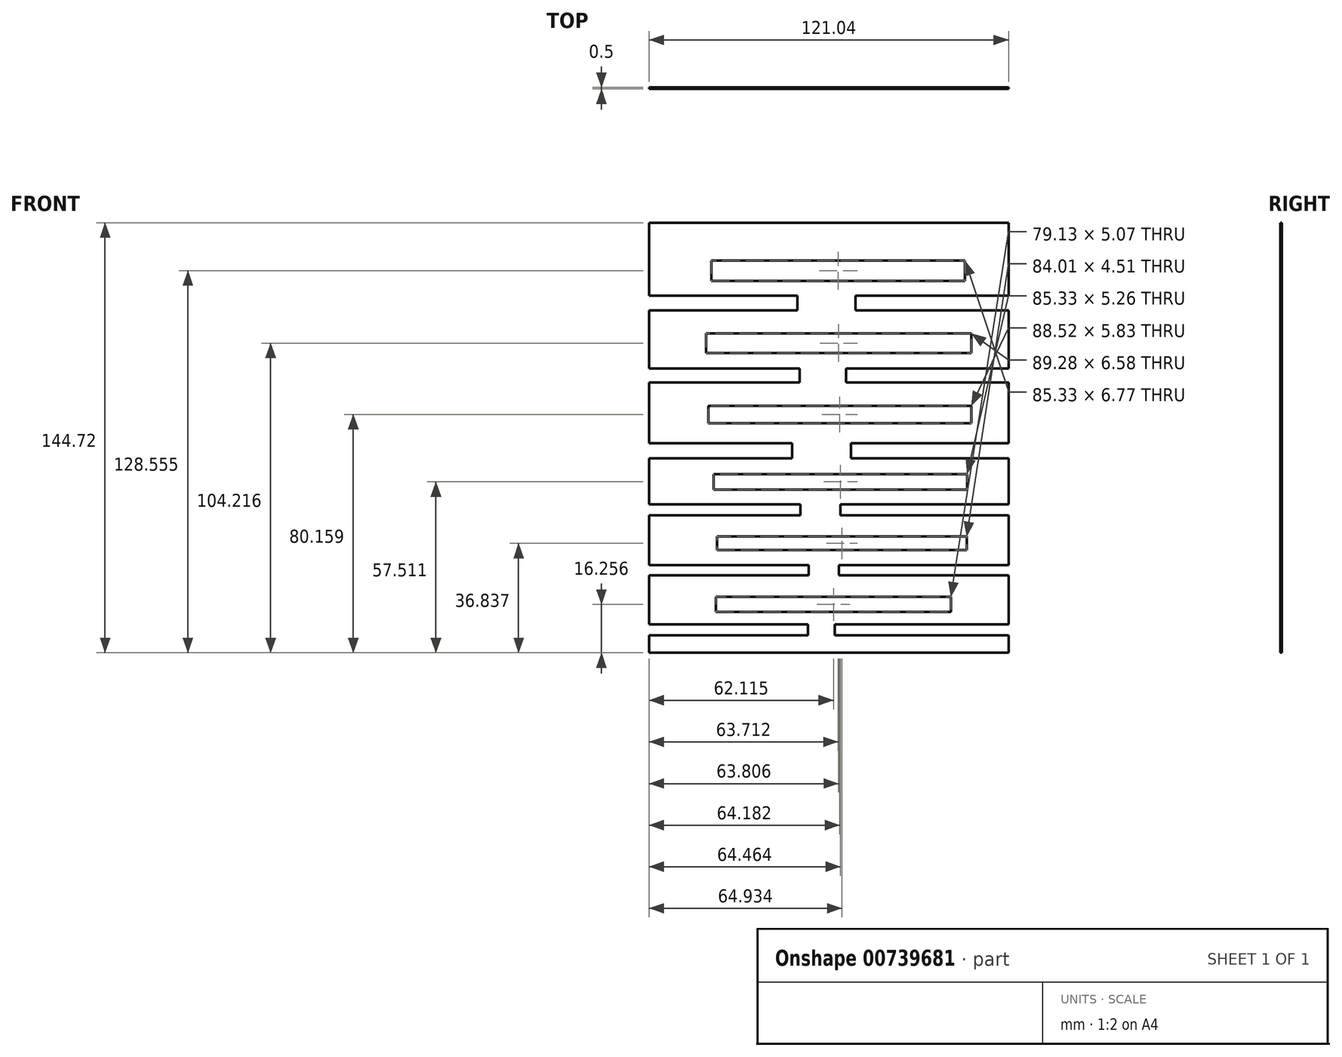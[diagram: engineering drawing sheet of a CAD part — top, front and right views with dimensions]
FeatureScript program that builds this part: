
annotation { "Feature Type Name" : "Feature", "Feature Type Description" : "" }
export const myFeature = defineFeature(function(context is Context, id is Id, definition is map)
    precondition{}
    {
        {
            var Q0;
            Q0=qCreatedBy(makeId("Front.planeOp"),FACE);
            var sketch = newSketch(context, id + "F0", { "sketchPlane" : qUnion([Q0])});
            skLineSegment(sketch, "E0.bottom", {"start": v(-58.36, 71.9) * mm, "end": v(62.68, 71.9) * mm});
            skLineSegment(sketch, "E0.top", {"start": v(-58.36, -72.82) * mm, "end": v(62.68, -72.82) * mm});
            skLineSegment(sketch, "E0.left", {"start": v(-58.36, 71.9) * mm, "end": v(-58.36, 47.37) * mm});
            skLineSegment(sketch, "E0.right", {"start": v(62.68, 71.9) * mm, "end": v(62.68, 47.37) * mm});
            skLineSegment(sketch, "E1.bottom", {"start": v(-58.36, -63.24) * mm, "end": v(-4.8, -63.24) * mm});
            skLineSegment(sketch, "E1.top", {"start": v(-58.36, -67) * mm, "end": v(-4.8, -67) * mm});
            skLineSegment(sketch, "E2", {"start": v(-4.8, -63.24) * mm, "end": v(-4.8, -67) * mm});
            skLineSegment(sketch, "E3", {"start": v(4.22, -63.24) * mm, "end": v(4.22, -67) * mm});
            skLineSegment(sketch, "E4.trimOffspring", {"start": v(4.22, -67) * mm, "end": v(62.68, -67) * mm});
            skLineSegment(sketch, "E5.trimOffspring", {"start": v(4.22, -63.24) * mm, "end": v(62.68, -63.24) * mm});
            skLineSegment(sketch, "E6.trimOffspring", {"start": v(-58.36, -67) * mm, "end": v(-58.36, -72.82) * mm});
            skLineSegment(sketch, "E7.trimOffspring", {"start": v(62.68, -67) * mm, "end": v(62.68, -72.82) * mm});
            skLineSegment(sketch, "E8.bottom", {"start": v(-35.8, -54.03) * mm, "end": v(43.32, -54.03) * mm});
            skLineSegment(sketch, "E8.top", {"start": v(-35.8, -59.1) * mm, "end": v(43.32, -59.1) * mm});
            skLineSegment(sketch, "E8.left", {"start": v(-35.8, -54.03) * mm, "end": v(-35.8, -59.1) * mm});
            skLineSegment(sketch, "E8.right", {"start": v(43.32, -54.03) * mm, "end": v(43.32, -59.1) * mm});
            skLineSegment(sketch, "E9.bottom", {"start": v(-58.36, -46.7) * mm, "end": v(-4.6, -46.7) * mm});
            skLineSegment(sketch, "E9.top", {"start": v(-58.36, -43.31) * mm, "end": v(-4.6, -43.31) * mm});
            skLineSegment(sketch, "E10", {"start": v(-4.6, -43.31) * mm, "end": v(-4.6, -46.7) * mm});
            skLineSegment(sketch, "E11", {"start": v(5.54, -43.31) * mm, "end": v(5.54, -46.7) * mm});
            skLineSegment(sketch, "E12.trimOffspring", {"start": v(5.54, -46.7) * mm, "end": v(62.68, -46.7) * mm});
            skLineSegment(sketch, "E13.trimOffspring", {"start": v(5.54, -43.31) * mm, "end": v(62.68, -43.31) * mm});
            skLineSegment(sketch, "E14.trimOffspring", {"start": v(-58.36, -46.7) * mm, "end": v(-58.36, -63.24) * mm});
            skLineSegment(sketch, "E15.trimOffspring", {"start": v(62.68, -46.7) * mm, "end": v(62.68, -63.24) * mm});
            skLineSegment(sketch, "E16.bottom", {"start": v(-35.43, -33.73) * mm, "end": v(48.58, -33.73) * mm});
            skLineSegment(sketch, "E16.top", {"start": v(-35.43, -38.24) * mm, "end": v(48.58, -38.24) * mm});
            skLineSegment(sketch, "E16.left", {"start": v(-35.43, -33.73) * mm, "end": v(-35.43, -38.24) * mm});
            skLineSegment(sketch, "E16.right", {"start": v(48.58, -33.73) * mm, "end": v(48.58, -38.24) * mm});
            skLineSegment(sketch, "E17.bottom", {"start": v(-58.36, -26.59) * mm, "end": v(-7.43, -26.59) * mm});
            skLineSegment(sketch, "E17.top", {"start": v(-58.36, -22.83) * mm, "end": v(-7.43, -22.83) * mm});
            skLineSegment(sketch, "E18", {"start": v(-7.43, -22.83) * mm, "end": v(-7.43, -26.59) * mm});
            skLineSegment(sketch, "E19", {"start": v(6.1, -22.83) * mm, "end": v(6.1, -26.59) * mm});
            skLineSegment(sketch, "E20.trimOffspring", {"start": v(6.1, -26.59) * mm, "end": v(62.68, -26.59) * mm});
            skLineSegment(sketch, "E21.trimOffspring", {"start": v(6.1, -22.83) * mm, "end": v(62.68, -22.83) * mm});
            skLineSegment(sketch, "E22.trimOffspring", {"start": v(-58.36, -26.59) * mm, "end": v(-58.36, -43.31) * mm});
            skLineSegment(sketch, "E23.trimOffspring", {"start": v(62.68, -26.59) * mm, "end": v(62.68, -43.31) * mm});
            skLineSegment(sketch, "E24.bottom", {"start": v(-36.56, -12.68) * mm, "end": v(48.77, -12.68) * mm});
            skLineSegment(sketch, "E24.top", {"start": v(-36.56, -17.94) * mm, "end": v(48.77, -17.94) * mm});
            skLineSegment(sketch, "E24.left", {"start": v(-36.56, -12.68) * mm, "end": v(-36.56, -17.94) * mm});
            skLineSegment(sketch, "E24.right", {"start": v(48.77, -12.68) * mm, "end": v(48.77, -17.94) * mm});
            skLineSegment(sketch, "E25.bottom", {"start": v(-58.36, -2.34) * mm, "end": v(-10.25, -2.34) * mm});
            skLineSegment(sketch, "E25.top", {"start": v(-58.36, -7.42) * mm, "end": v(-10.25, -7.42) * mm});
            skLineSegment(sketch, "E26", {"start": v(-10.25, -2.34) * mm, "end": v(-10.25, -7.42) * mm});
            skLineSegment(sketch, "E27", {"start": v(9.68, -2.34) * mm, "end": v(9.68, -7.42) * mm});
            skLineSegment(sketch, "E28.trimOffspring", {"start": v(9.68, -7.42) * mm, "end": v(62.68, -7.42) * mm});
            skLineSegment(sketch, "E29.trimOffspring", {"start": v(9.68, -2.34) * mm, "end": v(62.68, -2.34) * mm});
            skLineSegment(sketch, "E30.trimOffspring", {"start": v(-58.36, -7.42) * mm, "end": v(-58.36, -22.83) * mm});
            skLineSegment(sketch, "E31.trimOffspring", {"start": v(62.68, -7.42) * mm, "end": v(62.68, -22.83) * mm});
            skLineSegment(sketch, "E32.bottom", {"start": v(-38.44, 10.25) * mm, "end": v(50.08, 10.25) * mm});
            skLineSegment(sketch, "E32.top", {"start": v(-38.44, 4.43) * mm, "end": v(50.08, 4.43) * mm});
            skLineSegment(sketch, "E32.left", {"start": v(-38.44, 10.25) * mm, "end": v(-38.44, 4.43) * mm});
            skLineSegment(sketch, "E32.right", {"start": v(50.08, 10.25) * mm, "end": v(50.08, 4.43) * mm});
            skLineSegment(sketch, "E33.bottom", {"start": v(-58.36, 22.84) * mm, "end": v(-7.62, 22.84) * mm});
            skLineSegment(sketch, "E33.top", {"start": v(-58.36, 18.15) * mm, "end": v(-7.62, 18.15) * mm});
            skLineSegment(sketch, "E34", {"start": v(-7.62, 22.84) * mm, "end": v(-7.62, 18.15) * mm});
            skLineSegment(sketch, "E35", {"start": v(7.98, 22.84) * mm, "end": v(7.98, 18.15) * mm});
            skLineSegment(sketch, "E36.trimOffspring", {"start": v(7.98, 18.15) * mm, "end": v(62.68, 18.15) * mm});
            skLineSegment(sketch, "E37.trimOffspring", {"start": v(7.98, 22.84) * mm, "end": v(62.68, 22.84) * mm});
            skLineSegment(sketch, "E38.trimOffspring", {"start": v(-58.36, 18.15) * mm, "end": v(-58.36, -2.34) * mm});
            skLineSegment(sketch, "E39.trimOffspring", {"start": v(62.68, 18.15) * mm, "end": v(62.68, -2.34) * mm});
            skLineSegment(sketch, "E40.bottom", {"start": v(-39.2, 34.68) * mm, "end": v(50.08, 34.68) * mm});
            skLineSegment(sketch, "E40.top", {"start": v(-39.2, 28.1) * mm, "end": v(50.08, 28.1) * mm});
            skLineSegment(sketch, "E40.left", {"start": v(-39.2, 34.68) * mm, "end": v(-39.2, 28.1) * mm});
            skLineSegment(sketch, "E40.right", {"start": v(50.08, 34.68) * mm, "end": v(50.08, 28.1) * mm});
            skLineSegment(sketch, "E41.bottom", {"start": v(-58.36, 47.37) * mm, "end": v(-8.37, 47.37) * mm});
            skLineSegment(sketch, "E41.top", {"start": v(-58.36, 42.4) * mm, "end": v(-8.37, 42.4) * mm});
            skLineSegment(sketch, "E42", {"start": v(-8.37, 47.37) * mm, "end": v(-8.37, 42.4) * mm});
            skLineSegment(sketch, "E43", {"start": v(11.18, 47.37) * mm, "end": v(11.18, 42.4) * mm});
            skLineSegment(sketch, "E44.trimOffspring", {"start": v(11.18, 42.4) * mm, "end": v(62.68, 42.4) * mm});
            skLineSegment(sketch, "E45.trimOffspring", {"start": v(11.18, 47.37) * mm, "end": v(62.68, 47.37) * mm});
            skLineSegment(sketch, "E46.trimOffspring", {"start": v(-58.36, 42.4) * mm, "end": v(-58.36, 22.84) * mm});
            skLineSegment(sketch, "E47.trimOffspring", {"start": v(62.68, 42.4) * mm, "end": v(62.68, 22.84) * mm});
            skLineSegment(sketch, "E48.bottom", {"start": v(-37.31, 59.12) * mm, "end": v(48.02, 59.12) * mm});
            skLineSegment(sketch, "E48.top", {"start": v(-37.31, 52.35) * mm, "end": v(48.02, 52.35) * mm});
            skLineSegment(sketch, "E48.left", {"start": v(-37.31, 59.12) * mm, "end": v(-37.31, 52.35) * mm});
            skLineSegment(sketch, "E48.right", {"start": v(48.02, 59.12) * mm, "end": v(48.02, 52.35) * mm});
            skSolve(sketch);
        }
        {
            var Q0;
            Q0 = qSketchRegion(id + "F0", true);
            extrude(context, id + "F1", {"entities" : qUnion([Q0]), "depth" : .5 * mm, "offsetDistance" : 25 * mm});
        }
    });
